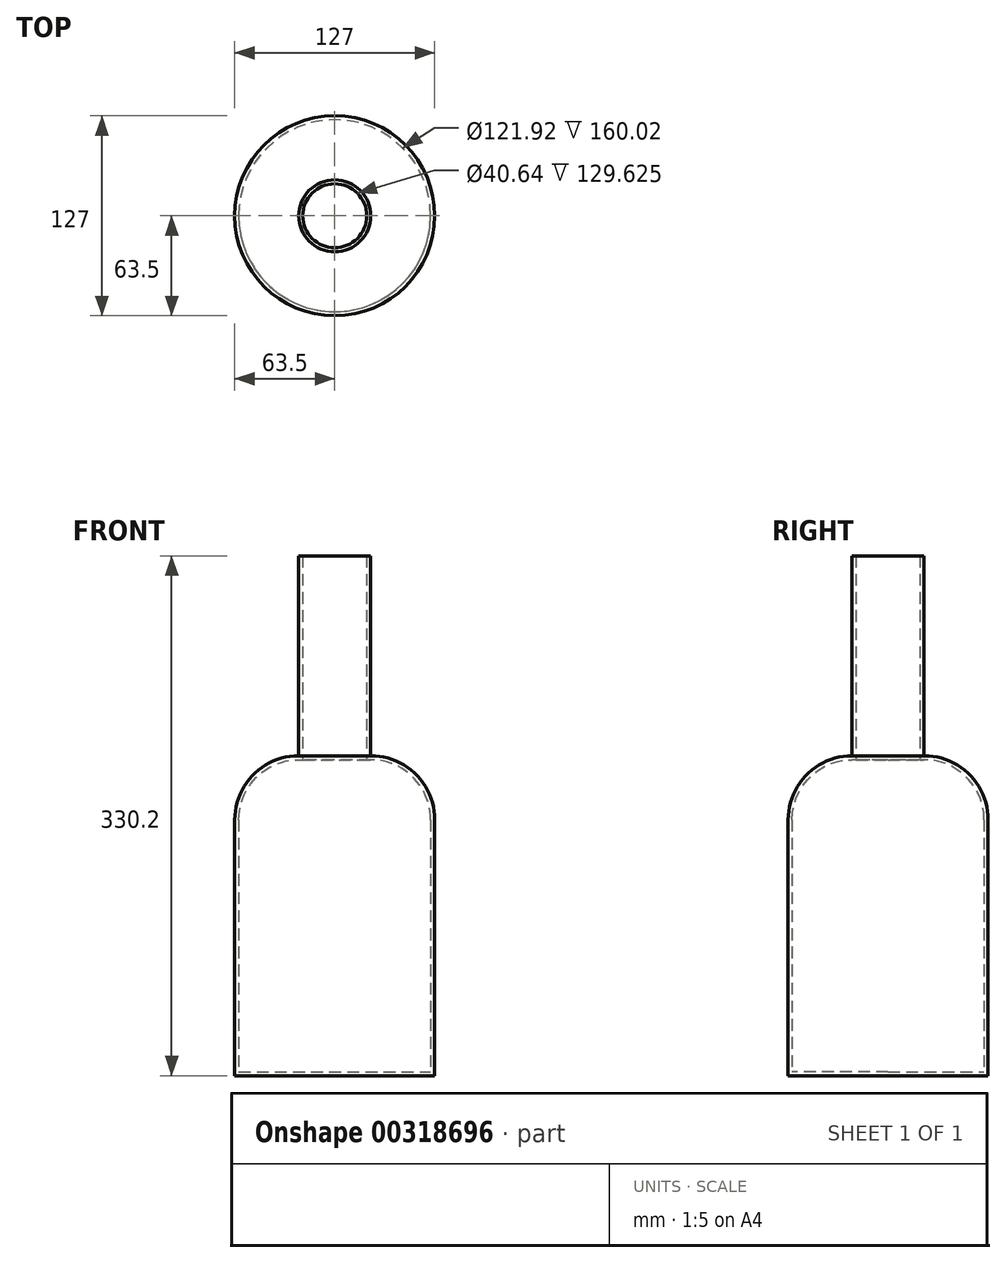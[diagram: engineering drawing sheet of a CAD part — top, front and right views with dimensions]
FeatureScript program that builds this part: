
annotation { "Feature Type Name" : "Feature", "Feature Type Description" : "" }
export const myFeature = defineFeature(function(context is Context, id is Id, definition is map)
    precondition{}
    {
        {
            var Q0;
            Q0=qCreatedBy(makeId("Top.planeOp"),FACE);
            var sketch = newSketch(context, id + "F0", { "sketchPlane" : qUnion([Q0])});
            skCircle(sketch, "E0", {"center": v(0, 0) * mm, "radius": 63.5 * mm});
            skSolve(sketch);
        }
        {
            var Q0;
            Q0=makeQuery(id+"F0.imprint","IMPRINT",FACE,{"disambiguationData":[TD([[makeQuery(id+"F0.imprint","IMPRINT",EDGE,{"derivedFrom":sQuery(id+"F0.wireOp",EDGE,"E0")}),1.0]])]});
            extrude(context, id + "F1", {"entities" : qUnion([Q0]), "depth" : 203.2 * mm});
        }
        {
            var Q0;
            Q0=makeQuery(id+"F1.opExtrude","CAP_EDGE",EDGE,{"disambiguationData":[OSD([sQuery(id+"F0.wireOp",EDGE,"E0")])],"isStart":false});
            fillet(context, id + "F2", {"entities" : qUnion([Q0]), "radius" : 40.64 * mm, "tangentPropagation" : true, "allowEdgeOverflow" : false});
        }
        {
            var Q0;
            Q0=makeQuery(id+"F1.opExtrude","CAP_FACE",FACE,{"disambiguationData":[OSD([sQuery(id+"F0.wireOp",EDGE,"E0")])],"isStart":false});
            extrude(context, id + "F3", {"entities" : qUnion([Q0]), "operationType" : NewBodyOperationType.ADD, "depth" : 127 * mm});
        }
        {
            var Q0;
            Q0=makeQuery(id+"F3.opExtrude","CAP_FACE",FACE,{"disambiguationData":[OSD([sQuery(id+"F0.wireOp",EDGE,"E0")])],"isStart":false});
            shell(context, id + "F4", {"entities" : qUnion([Q0]), "thickness" : 2.54 * mm});
        }
    });
